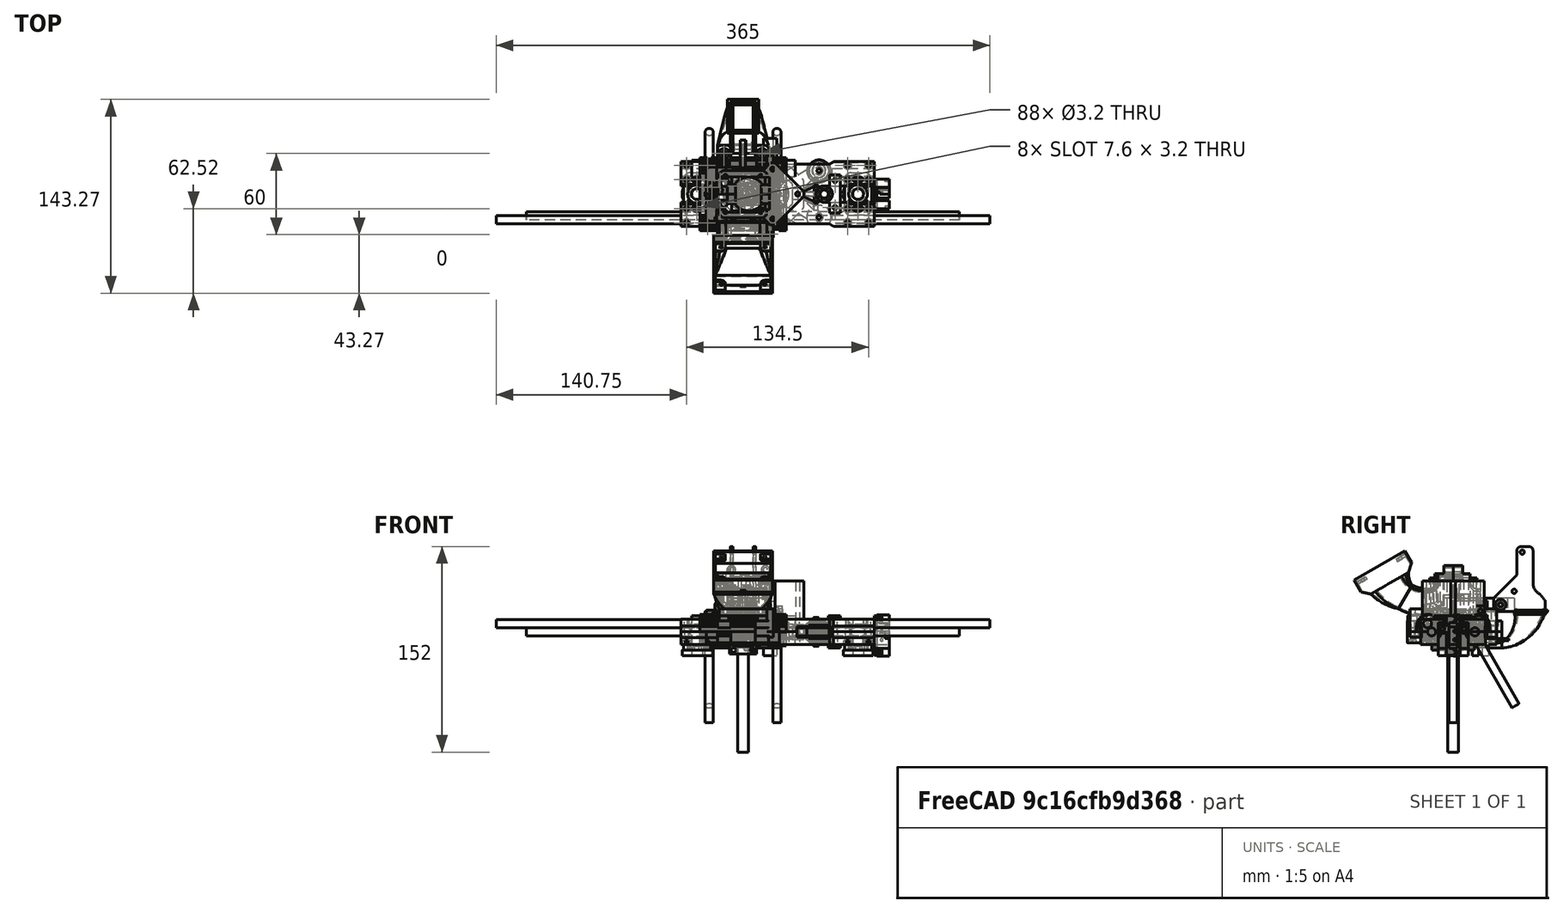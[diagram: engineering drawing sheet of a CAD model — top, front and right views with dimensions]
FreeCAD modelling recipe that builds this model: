
FCSTD DOCUMENT  (FreeCAD 0.18R15441 (Git))
Label: XZAxis_Assembly_A2PlusAddon
License: All rights reserved
LicenseURL: http://en.wikipedia.org/wiki/All_rights_reserved
objects: Part::FeaturePython×55, Part::Mirroring×15, App::Part×10, Part::Cylinder×5
note: 75 computed .brp shape members not serialized (recipe doc carries the construction recipe); baked Part::Feature solids carry a one-line shape summary decoded from their .brp

FEATURE [Part::FeaturePython] RightXEndHalf_Bottom_001  label="RightXEndHalf_Bottom"  # a2plus imported part (geometry in sourceFile) (typed FeaturePython)
  Placement = pos=(0,0,0) rot=(0,0,1;3.14159rad)
  a2p_Version = V0.1
  fixedPosition = true
  sourceFile = ./XAxis_Right/RightXEndHalf_Bottom.FCStd
  subassemblyImport = false
  timeLastImport = 1.54791e+09
  updateColors = true
FEATURE [Part::FeaturePython] RightXEndHalf_001  label="RightXEndHalf_Top"  # a2plus imported part (geometry in sourceFile) (typed FeaturePython)
  Placement = pos=(0,0,0) rot=(0,1,0;3.14159rad)
  a2p_Version = V0.1
  fixedPosition = true
  sourceFile = ./XAxis_Right/RightXEndHalf_Top.FCStd
  subassemblyImport = false
  timeLastImport = 1.54791e+09
  updateColors = true
FEATURE [Part::FeaturePython] RightXEnd_TensionerIdler_001  label="RightXEnd_TensionerIdler"  # a2plus imported part (geometry in sourceFile) (typed FeaturePython)
  a2p_Version = V0.1
  fixedPosition = true
  sourceFile = ./XAxis_Right/RightXEnd_TensionerIdler.FCStd
  subassemblyImport = false
  timeLastImport = 1.54602e+09
  updateColors = true
FEATURE [Part::FeaturePython] RightXEnd_TensionerKnob_001  label="RightXEnd_TensionerKnob"  # a2plus imported part (geometry in sourceFile) (typed FeaturePython)
  Placement = pos=(45.5,0,3.1e-15) rot=(0,1,0;1.5708rad)
  a2p_Version = V0.1
  fixedPosition = true
  sourceFile = ./XAxis_Right/RightXEnd_TensionerKnob.FCStd
  subassemblyImport = false
  timeLastImport = 1.54006e+09
  updateColors = true
FEATURE [Part::FeaturePython] RightXEnd_TensionerStand_001  label="RightXEnd_TensionerStand"  # a2plus imported part (geometry in sourceFile) (typed FeaturePython)
  Placement = pos=(36.825,-5e-15,0) rot=(0,0,1;3.14159rad)
  a2p_Version = V0.1
  fixedPosition = true
  sourceFile = ./XAxis_Right/RightXEnd_TensionerStand.FCStd
  subassemblyImport = false
  timeLastImport = 1.54596e+09
  updateColors = true
FEATURE [Part::FeaturePython] BeltPulley_2x685zz_FCGearAddon_001  label="BeltPulley_2x685zz_FCGearAddon"  # a2plus imported part (geometry in sourceFile) (typed FeaturePython)
  Placement = pos=(4,0,-3.5) rot=(0,0,1;0rad)
  a2p_Version = V0.1
  fixedPosition = true
  sourceFile = ./XAxis_Right/BeltPulley_2x685zz_FCGearAddon.FCStd
  subassemblyImport = false
  timeLastImport = 1.54006e+09
  updateColors = true
FEATURE [App::Part] Part001  label="RightIdlerPart"
  Group = -> [RightXEnd_TensionerIdler_001,BeltPulley_2x685zz_FCGearAddon_001]
  Origin = -> Origin001
  Placement = pos=(15,0,0) rot=(0,0,1;0rad)
FEATURE [Part::FeaturePython] BeltPulley_2x623zz_FCGearAddon_001  label="Right_BeltPulley_2x623zz_FCGearAddon"  # a2plus imported part (geometry in sourceFile) (typed FeaturePython)
  Placement = pos=(-5,-17.25,-3.25) rot=(0,0,1;0rad)
  a2p_Version = V0.1
  fixedPosition = true
  sourceFile = ./XAxis_Right/BeltPulley_2x623zz_FCGearAddon.FCStd
  subassemblyImport = false
  timeLastImport = 1.54602e+09
  updateColors = true
FEATURE [Part::Mirroring] Part__Mirroring  label="Right_BeltPulley_2x623zz_FCGearAddon_Mirror"
  Base = (0,0,0)
  Normal = (0,1,0)
  Source = -> BeltPulley_2x623zz_FCGearAddon_001
FEATURE [Part::FeaturePython] Rod_M6x320mm_001  label="XRod_M6x320mm"  # a2plus imported part (geometry in sourceFile) (typed FeaturePython)
  Placement = pos=(0,16,0) rot=(-1,0,0;1.5708rad)
  a2p_Version = V0.1
  fixedPosition = false
  sourceFile = ./Helpers/Rod_M6x320mm.FCStd
  subassemblyImport = false
  timeLastImport = 1.54611e+09
  updateColors = true
FEATURE [Part::Mirroring] Part__Mirroring001  label="XRod_M6x320mm_Mirror"
  Base = (0,0,0)
  Normal = (0,1,0)
  Source = -> Rod_M6x320mm_001
FEATURE [App::Part] Part003  label="XRods"
  Group = -> [Rod_M6x320mm_001,Part__Mirroring001]
  Origin = -> Origin003
FEATURE [Part::FeaturePython] LeftXEndHalf_Bottom_001  label="LeftXEndHalf_Bottom"  # a2plus imported part (geometry in sourceFile) (typed FeaturePython)
  a2p_Version = V0.1
  fixedPosition = false
  sourceFile = ./XAxis_Left/LeftXEndHalf_Bottom.FCStd
  subassemblyImport = false
  timeLastImport = 1.54791e+09
  updateColors = true
FEATURE [Part::FeaturePython] LeftXEndHalf_001  label="LeftXEndHalf_Top"  # a2plus imported part (geometry in sourceFile) (typed FeaturePython)
  Placement = pos=(0,0,0) rot=(1,0,0;3.14159rad)
  a2p_Version = V0.1
  fixedPosition = false
  sourceFile = ./XAxis_Left/LeftXEndHalf_Top.FCStd
  subassemblyImport = false
  timeLastImport = 1.54791e+09
  updateColors = true
FEATURE [Part::FeaturePython] BeltPulley_2x623zz_FCGearAddon_002  label="Left_BeltPulley_2x623zz_FCGearAddon"  # a2plus imported part (geometry in sourceFile) (typed FeaturePython)
  Placement = pos=(56.125,-17.25,-3.25) rot=(0,0,1;0rad)
  a2p_Version = V0.1
  fixedPosition = false
  sourceFile = ./XAxis_Right/BeltPulley_2x623zz_FCGearAddon.FCStd
  subassemblyImport = false
  timeLastImport = 1.54602e+09
  updateColors = true
FEATURE [Part::Mirroring] Part__Mirroring002  label="Left_BeltPulley_2x623zz_FCGearAddon (Mirror #3)"
  Base = (0,0,0)
  Normal = (0,1,0)
  Source = -> BeltPulley_2x623zz_FCGearAddon_002
FEATURE [Part::FeaturePython] CarriageHalf_Bottom_001  label="XCarriageHalf_Bottom"  # a2plus imported part (geometry in sourceFile) (typed FeaturePython)
  Placement = pos=(0,-1e-15,-8) rot=(1,0,0;3.14159rad)
  a2p_Version = V0.1
  fixedPosition = false
  sourceFile = ./XCarriage/CarriageHalf_Bottom.FCStd
  subassemblyImport = false
  timeLastImport = 1.54527e+09
  updateColors = true
FEATURE [Part::FeaturePython] CarriageHalf_001  label="XCarriageHalf_Top"  # a2plus imported part (geometry in sourceFile) (typed FeaturePython)
  Placement = pos=(0,0,8) rot=(0,0,1;3.14159rad)
  a2p_Version = V0.1
  fixedPosition = false
  sourceFile = ./XCarriage/CarriageHalf_Top.FCStd
  subassemblyImport = false
  timeLastImport = 1.54774e+09
  updateColors = true
FEATURE [Part::FeaturePython] LM6UU_IGUS_001  label="XBearing"  # a2plus imported part (geometry in sourceFile) (typed FeaturePython)
  Placement = pos=(-20.25,-16,-4e-15) rot=(0,1,0;1.5708rad)
  a2p_Version = V0.1
  fixedPosition = false
  sourceFile = ./Other/LM6UU_IGUS.fcstd
  subassemblyImport = false
  timeLastImport = 1.54524e+09
  updateColors = true
FEATURE [Part::Mirroring] Part__Mirroring003  label="XBearing_Mirror1_YZ"
  Base = (0,0,0)
  Normal = (1,0,0)
  Source = -> LM6UU_IGUS_001
FEATURE [Part::Mirroring] Part__Mirroring004  label="XBearing_Mirror1_XZ"
  Base = (0,0,0)
  Normal = (0,1,0)
  Source = -> LM6UU_IGUS_001
FEATURE [Part::Mirroring] Part__Mirroring005  label="XBearing_Mirror2_XZ"
  Base = (0,0,0)
  Normal = (0,1,0)
  Source = -> Part__Mirroring003
FEATURE [Part::FeaturePython] CarriageBeltClamp_001  label="XCarriageBeltClamp"  # a2plus imported part (geometry in sourceFile) (typed FeaturePython)
  Placement = pos=(-19,-34,-3) rot=(0,0,1;0rad)
  a2p_Version = V0.1
  fixedPosition = false
  sourceFile = ./XCarriage/CarriageBeltClamp.FCStd
  subassemblyImport = false
  timeLastImport = 1.54006e+09
  updateColors = true
FEATURE [Part::Mirroring] Part__Mirroring006  label="XCarriageBeltClamp_Mirror"
  Base = (0,0,0)
  Normal = (1,0,0)
  Source = -> CarriageBeltClamp_001
FEATURE [Part::FeaturePython] BearingClamp_001  label="LeftBearingClamp"  # a2plus imported part (geometry in sourceFile) (typed FeaturePython)
  Placement = pos=(66.1,0,0) rot=(0,0,1;0rad)
  a2p_Version = V0.1
  fixedPosition = false
  sourceFile = ./XAxis_Left/BearingClamp.FCStd
  subassemblyImport = false
  timeLastImport = 1.54786e+09
  updateColors = true
FEATURE [Part::FeaturePython] LeftBearingClamp_001  label="RightBearingClamp"  # a2plus imported part (geometry in sourceFile) (typed FeaturePython)
  Placement = pos=(-15.1,2e-15,0) rot=(0,0,1;3.14159rad)
  a2p_Version = V0.1
  fixedPosition = false
  sourceFile = ./XAxis_Left/BearingClamp.FCStd
  subassemblyImport = false
  timeLastImport = 1.54786e+09
  updateColors = true
FEATURE [Part::FeaturePython] HotendClippingLeftHalf_E3DV6_Bowden_001  label="HotendClippingLeftHalf_E3DV6_Bowden"  # a2plus imported part (geometry in sourceFile) (typed FeaturePython)
  Placement = pos=(0,0,8) rot=(0,0,1;0rad)
  a2p_Version = V0.1
  fixedPosition = false
  sourceFile = ./XCarriage/HotendClippingLeftHalf_E3DV6_Bowden.FCStd
  subassemblyImport = false
  timeLastImport = 1.54672e+09
  updateColors = true
FEATURE [Part::FeaturePython] HotendClippingRightHalf_E3DV6_Bowden_001  label="HotendClippingRightHalf_E3DV6_Bowden"  # a2plus imported part (geometry in sourceFile) (typed FeaturePython)
  Placement = pos=(0,0,8) rot=(0,0,1;0rad)
  a2p_Version = V0.1
  fixedPosition = false
  sourceFile = ./XCarriage/HotendClippingRightHalf_E3DV6_Bowden.FCStd
  subassemblyImport = false
  timeLastImport = 1.54679e+09
  updateColors = true
FEATURE [Part::FeaturePython] Hotend_E3D_Dummy_001  label="Hotend_E3D_Dummy"  # a2plus imported part (geometry in sourceFile) (typed FeaturePython)
  Placement = pos=(4,0,11.3) rot=(0,0,1;0rad)
  a2p_Version = V0.1
  fixedPosition = false
  sourceFile = ./Helpers/Hotend_E3D_Dummy.FCStd
  subassemblyImport = false
  timeLastImport = 1.54646e+09
  updateColors = true
FEATURE [Part::FeaturePython] Hotend_E3D_Dummy_Outer_001  label="Hotend_E3D_Dummy_Outer"  # a2plus imported part (geometry in sourceFile) (typed FeaturePython)
  Placement = pos=(4,0,11.3) rot=(0,0,1;0rad)
  a2p_Version = V0.1
  fixedPosition = false
  sourceFile = ./Helpers/Hotend_E3D_Dummy_Outer.FCStd
  subassemblyImport = false
  timeLastImport = 1.54656e+09
  updateColors = true
FEATURE [Part::Cylinder] Cylinder  label="ScrewTopCilinder1"
  Angle = 360
  AttacherType = Attacher::AttachEngine3D
  Height = 4
  Placement = pos=(-14,-30,8) rot=(0,0,1;0rad)
  Radius = 3.5
FEATURE [Part::Cylinder] Cylinder001  label="ScrewTopCilinder2"
  Angle = 360
  AttacherType = Attacher::AttachEngine3D
  Height = 4
  Placement = pos=(14,-30,8) rot=(0,0,1;0rad)
  Radius = 3.5
FEATURE [Part::FeaturePython] HotendFrontFanCase_40x40_001  label="HotendFrontFanCase_40x40"  # a2plus imported part (geometry in sourceFile) (typed FeaturePython)
  Placement = pos=(0,-21,21) rot=(0,0,1;0rad)
  a2p_Version = V0.1
  fixedPosition = false
  sourceFile = ./XCarriage/HotendFrontFanCase_40x40.FCStd
  subassemblyImport = false
  timeLastImport = 1.54722e+09
  updateColors = true
FEATURE [Part::FeaturePython] FrontFanCaseClip_40x40_001  label="FrontFanCaseClip_40x40"  # a2plus imported part (geometry in sourceFile) (typed FeaturePython)
  Placement = pos=(0,-20,21) rot=(0,0,1;3.14159rad)
  a2p_Version = V0.1
  fixedPosition = false
  sourceFile = ./XCarriage/FrontFanCaseClip_40x40.FCStd
  subassemblyImport = false
  timeLastImport = 1.54722e+09
  updateColors = true
FEATURE [Part::FeaturePython] BackClip_001  label="BackClip"  # a2plus imported part (geometry in sourceFile) (typed FeaturePython)
  Placement = pos=(2e-15,20,15) rot=(0,0,1;3.14159rad)
  a2p_Version = V0.1
  fixedPosition = false
  sourceFile = ./XCarriage/BackClip.FCStd
  subassemblyImport = false
  timeLastImport = 1.54724e+09
  updateColors = true
FEATURE [Part::FeaturePython] BackTurbineClip_001  label="BackTurbineClip"  # a2plus imported part (geometry in sourceFile) (typed FeaturePython)
  Placement = pos=(4e-15,30,15) rot=(0,0,1;3.14159rad)
  a2p_Version = V0.1
  fixedPosition = false
  sourceFile = ./XCarriage/BackTurbineClip.FCStd
  subassemblyImport = false
  timeLastImport = 1.54726e+09
  updateColors = true
FEATURE [Part::FeaturePython] BackTurbinePipe_TwoSides_001  label="BackTurbinePipe_TwoSides"  # a2plus imported part (geometry in sourceFile) (typed FeaturePython)
  Placement = pos=(4e-15,30,15) rot=(0,0,1;3.14159rad)
  a2p_Version = V0.1
  fixedPosition = false
  sourceFile = ./XCarriage/BackTurbinePipe_TwoSides.FCStd
  subassemblyImport = false
  timeLastImport = 1.54847e+09
  updateColors = true
FEATURE [App::Part] Part005  label="XCarriage"
  Group = -> [CarriageHalf_Bottom_001,CarriageHalf_001,LM6UU_IGUS_001,Part__Mirroring003,Part__Mirroring005,Part__Mirroring004,CarriageBeltClamp_001,Part__Mirroring006,HotendClippingLeftHalf_E3DV6_Bowden_001,HotendClippingRightHalf_E3DV6_Bowden_001,Hotend_E3D_Dummy_001,Hotend_E3D_Dummy_Outer_001,Cylinder,Cylinder001,HotendFrontFanCase_40x40_001,FrontFanCaseClip_40x40_001,BackClip_001,BackTurbineClip_001,+1 more]
  Origin = -> Origin005
FEATURE [Part::FeaturePython] ZThreaderRodClip_THSL_200_8D_001  label="LeftZThreaderRodClip_THSL-200-8D"  # a2plus imported part (geometry in sourceFile) (typed FeaturePython)
  Placement = pos=(85,0,-13.5) rot=(0,0,1;0rad)
  a2p_Version = V0.1
  fixedPosition = false
  sourceFile = ./XAxis_Left/ZThreaderRodClip_THSL-200-8D.FCStd
  subassemblyImport = false
  timeLastImport = 1.54751e+09
  updateColors = true
FEATURE [Part::FeaturePython] ZThreaderRodClip_THSL_200_8D_001001  label="RightZThreaderRodClip_THSL-200-8D"  # a2plus imported part (geometry in sourceFile) (typed FeaturePython)
  Placement = pos=(-34,0,-13.5) rot=(0,0,1;0rad)
  a2p_Version = V0.1
  fixedPosition = false
  sourceFile = ./XAxis_Left/ZThreaderRodClip_THSL-200-8D.FCStd
  subassemblyImport = false
  timeLastImport = 1.54751e+09
  updateColors = true
FEATURE [Part::FeaturePython] THSL_200_8D_001  label="LeftNut_THSL-200-8D"  # a2plus imported part (geometry in sourceFile) (typed FeaturePython)
  Placement = pos=(85,0,-17.5) rot=(0,0,1;0rad)
  a2p_Version = V0.1
  fixedPosition = false
  sourceFile = ./Helpers/THSL-200-8D_Nut.FCStd
  subassemblyImport = false
  timeLastImport = 1.54757e+09
  updateColors = true
FEATURE [Part::FeaturePython] LeftNut_THSL_200_8D_001  label="RightNut_THSL-200-8D"  # a2plus imported part (geometry in sourceFile) (typed FeaturePython)
  Placement = pos=(-34,0,-17.5) rot=(0,0,1;0rad)
  a2p_Version = V0.1
  fixedPosition = false
  sourceFile = ./Helpers/THSL-200-8D_Nut.FCStd
  subassemblyImport = false
  timeLastImport = 1.54757e+09
  updateColors = true
FEATURE [Part::FeaturePython] XBearing_001  label="RightZBearing"  # a2plus imported part (geometry in sourceFile) (typed FeaturePython)
  Placement = pos=(-9,0,-5e-15) rot=(0,0,1;0rad)
  a2p_Version = V0.1
  fixedPosition = false
  sourceFile = ./Other/LM6UU_IGUS.fcstd
  subassemblyImport = false
  timeLastImport = 1.54524e+09
  updateColors = true
FEATURE [Part::FeaturePython] RightZBearing_001  label="LeftZBearing"  # a2plus imported part (geometry in sourceFile) (typed FeaturePython)
  Placement = pos=(60,0,0) rot=(0,0,1;0rad)
  a2p_Version = V0.1
  fixedPosition = false
  sourceFile = ./Other/LM6UU_IGUS.fcstd
  subassemblyImport = false
  timeLastImport = 1.54524e+09
  updateColors = true
FEATURE [Part::FeaturePython] Huxley_Z_Motor_Bracket_001  label="RightMotorBracket"  # a2plus imported part (geometry in sourceFile) (typed FeaturePython)
  Placement = pos=(-18,-27.05,0) rot=(0,0,1;0rad)
  a2p_Version = V0.1
  fixedPosition = false
  sourceFile = ./Helpers/Huxley_Z_Motor_Bracket.FCStd
  subassemblyImport = false
  timeLastImport = 1.54757e+09
  updateColors = true
FEATURE [Part::FeaturePython] Nema14_Motor_001  label="RightMotor"  # a2plus imported part (geometry in sourceFile) (typed FeaturePython)
  Placement = pos=(0,1e-15,12) rot=(1,0,0;3.14159rad)
  a2p_Version = V0.1
  fixedPosition = false
  sourceFile = ./Helpers/Nema14_Motor.FCStd
  subassemblyImport = false
  timeLastImport = 1.54757e+09
  updateColors = true
FEATURE [Part::FeaturePython] Right_Motor_001  label="XMotor"  # a2plus imported part (geometry in sourceFile) (typed FeaturePython)
  Placement = pos=(21.885,2e-15,9.5) rot=(0.382683,0.92388,0;3.14159rad)
  a2p_Version = V0.1
  fixedPosition = false
  sourceFile = ./Helpers/Nema14_Motor.FCStd
  subassemblyImport = false
  timeLastImport = 1.54757e+09
  updateColors = true
FEATURE [Part::FeaturePython] Huxley_TopFrameVertex_001  label="RightFrameVertex"  # a2plus imported part (geometry in sourceFile) (typed FeaturePython)
  Placement = pos=(-32,-19.0525,6.00011) rot=(-0.250563,0.935113,-0.250563;1.63783rad)
  a2p_Version = V0.1
  fixedPosition = false
  sourceFile = ./Helpers/Huxley_TopFrameVertex.FCStd
  subassemblyImport = false
  timeLastImport = 1.54758e+09
  updateColors = true
FEATURE [Part::FeaturePython] Rod_M6x365mm_001  label="Top_Rod_M6x365mm"  # a2plus imported part (geometry in sourceFile) (typed FeaturePython)
  Placement = pos=(0,19.05,6) rot=(-1,0,0;1.5708rad)
  a2p_Version = V0.1
  fixedPosition = false
  sourceFile = ./Helpers/Rod_M6x365mm.FCStd
  subassemblyImport = false
  timeLastImport = 1.54758e+09
  updateColors = true
FEATURE [Part::Mirroring] Part__Mirroring007  label="Top_Rod_M6x365mm_Mirror"
  Base = (0,0,0)
  Normal = (0,1,0)
  Source = -> Rod_M6x365mm_001
FEATURE [App::Part] Part008  label="TopRods"
  Group = -> [Rod_M6x365mm_001,Part__Mirroring007]
  Origin = -> Origin008
  Placement = pos=(0,0,30) rot=(0,0,1;0rad)
FEATURE [Part::FeaturePython] Huxley_Z_Motor_Bracket_002  label="LeftMotorBracket"  # a2plus imported part (geometry in sourceFile) (typed FeaturePython)
  Placement = pos=(18,27.05,0) rot=(0,0,1;3.14159rad)
  a2p_Version = V0.1
  fixedPosition = false
  sourceFile = ./Helpers/Huxley_Z_Motor_Bracket.FCStd
  subassemblyImport = false
  timeLastImport = 1.54757e+09
  updateColors = true
FEATURE [Part::FeaturePython] Huxley_TopFrameVertex_002  label="LeftFrameVertex"  # a2plus imported part (geometry in sourceFile) (typed FeaturePython)
  Placement = pos=(32,19.05,6) rot=(-0.694747,-0.186157,0.694747;2.7735rad)
  a2p_Version = V0.1
  fixedPosition = false
  sourceFile = ./Helpers/Huxley_TopFrameVertex.FCStd
  subassemblyImport = false
  timeLastImport = 1.54758e+09
  updateColors = true
FEATURE [Part::FeaturePython] Nema14_Motor_002  label="LeftMotor"  # a2plus imported part (geometry in sourceFile) (typed FeaturePython)
  Placement = pos=(0,1e-15,12) rot=(1,0,0;3.14159rad)
  a2p_Version = V0.1
  fixedPosition = false
  sourceFile = ./Helpers/Nema14_Motor.FCStd
  subassemblyImport = false
  timeLastImport = 1.54757e+09
  updateColors = true
FEATURE [Part::Cylinder] Cylinder002  label="LeftTopRodNut"
  Angle = 360
  AttacherType = Attacher::AttachEngine3D
  Height = 6.5
  Placement = pos=(32,-19.05,6) rot=(0,1,0;1.5708rad)
  Radius = 6
FEATURE [Part::Mirroring] Part__Mirroring008  label="LeftTopRodNut_Mirror"
  Base = (0,0,0)
  Normal = (0,1,0)
  Source = -> Cylinder002
FEATURE [Part::Cylinder] Cylinder003  label="RightTopRodNut"
  Angle = 360
  AttacherType = Attacher::AttachEngine3D
  Height = 6.5
  Placement = pos=(-38,-19.05,6) rot=(0,1,0;1.5708rad)
  Radius = 6
FEATURE [Part::Mirroring] Part__Mirroring009  label="RightTopRodNut_Mirror"
  Base = (0,0,0)
  Normal = (0,1,0)
  Source = -> Cylinder003
FEATURE [Part::FeaturePython] Rod_M6x80mm_001  label="RightRod_M6x80mm"  # a2plus imported part (geometry in sourceFile) (typed FeaturePython)
  Placement = pos=(25,0,-27) rot=(0,1,0;1.5708rad)
  a2p_Version = V0.1
  fixedPosition = false
  sourceFile = ./Helpers/Rod_M6x80mm.FCStd
  subassemblyImport = false
  timeLastImport = 1.54757e+09
  updateColors = true
FEATURE [Part::FeaturePython] Rod_M6x80mm_002  label="LeftRod_M6x80mm"  # a2plus imported part (geometry in sourceFile) (typed FeaturePython)
  Placement = pos=(-25,0,-27) rot=(0,1,0;1.5708rad)
  a2p_Version = V0.1
  fixedPosition = false
  sourceFile = ./Helpers/Rod_M6x80mm.FCStd
  subassemblyImport = false
  timeLastImport = 1.54757e+09
  updateColors = true
FEATURE [Part::FeaturePython] Rod_M6x80mm_003  label="RightSideRod_M6x80mm"  # a2plus imported part (geometry in sourceFile) (typed FeaturePython)
  Placement = pos=(-25,-26.0167,-20.0622) rot=(-0.250563,0.935113,-0.250563;1.63783rad)
  a2p_Version = V0.1
  fixedPosition = false
  sourceFile = ./Helpers/Rod_M6x80mm.FCStd
  subassemblyImport = false
  timeLastImport = 1.54757e+09
  updateColors = true
FEATURE [Part::Mirroring] Part__Mirroring010  label="RightSideRod_M6x80mm_Mirror"
  Base = (0,0,0)
  Normal = (0,1,0)
  Source = -> Rod_M6x80mm_003
FEATURE [Part::FeaturePython] Rod_M6x80mm_004  label="LeftSideRod_M6x80mm"  # a2plus imported part (geometry in sourceFile) (typed FeaturePython)
  Placement = pos=(25,-26.0167,-20.0622) rot=(-0.250563,0.935113,-0.250563;1.63783rad)
  a2p_Version = V0.1
  fixedPosition = false
  sourceFile = ./Helpers/Rod_M6x80mm.FCStd
  subassemblyImport = false
  timeLastImport = 1.54757e+09
  updateColors = true
FEATURE [Part::Mirroring] Part__Mirroring011  label="LeftSideRod_M6x80mm_Mirror"
  Base = (0,0,0)
  Normal = (0,1,0)
  Source = -> Rod_M6x80mm_004
FEATURE [Part::FeaturePython] ZThreadedRodCoupler_THSL_200_8D_D8mm_001  label="RightZThreadedRodCoupler_THSL-200-8D"  # a2plus imported part (geometry in sourceFile) (typed FeaturePython)
  Placement = pos=(0,0,-16.5) rot=(0,0,1;0rad)
  a2p_Version = V0.1
  fixedPosition = false
  sourceFile = ./ZAxis/ZThreadedRodCoupler_THSL-200-8D_D8mm.FCStd
  subassemblyImport = false
  timeLastImport = 1.54006e+09
  updateColors = true
FEATURE [Part::Mirroring] Part__Mirroring012  label="RightZThreadedRodCoupler_THSL-200-8D_Mirror"
  Base = (0,0,0)
  Normal = (0,1,0)
  Source = -> ZThreadedRodCoupler_THSL_200_8D_D8mm_001
FEATURE [Part::FeaturePython] ZThreadedRodCoupler_THSL_200_8D_D8mm_002  label="LeftZThreadedRodCoupler_THSL-200-8D"  # a2plus imported part (geometry in sourceFile) (typed FeaturePython)
  Placement = pos=(0,0,-16.5) rot=(0,0,1;0rad)
  a2p_Version = V0.1
  fixedPosition = false
  sourceFile = ./ZAxis/ZThreadedRodCoupler_THSL-200-8D_D8mm.FCStd
  subassemblyImport = false
  timeLastImport = 1.54006e+09
  updateColors = true
FEATURE [Part::Mirroring] Part__Mirroring013  label="LeftZThreadedRodCoupler_THSL-200-8D_Mirror"
  Base = (0,0,0)
  Normal = (0,1,0)
  Source = -> ZThreadedRodCoupler_THSL_200_8D_D8mm_002
FEATURE [Part::FeaturePython] Rod_M8x80mm_001  label="LeftRod_M8x80mm"  # a2plus imported part (geometry in sourceFile) (typed FeaturePython)
  Placement = pos=(1.09e-14,0,-49) rot=(0,1,0;1.5708rad)
  a2p_Version = V0.1
  fixedPosition = false
  sourceFile = ./Helpers/Rod_M8x80mm.FCStd
  subassemblyImport = false
  timeLastImport = 1.54757e+09
  updateColors = true
FEATURE [App::Part] Part009  label="LeftMotorMount"
  Group = -> [Huxley_Z_Motor_Bracket_002,Nema14_Motor_002,Huxley_TopFrameVertex_002,Cylinder002,Part__Mirroring008,Rod_M6x80mm_002,Rod_M6x80mm_004,Part__Mirroring011,ZThreadedRodCoupler_THSL_200_8D_D8mm_002,Part__Mirroring013,Rod_M8x80mm_001]
  Origin = -> Origin009
  Placement = pos=(-141,0,30) rot=(0,0,1;0rad)
FEATURE [Part::FeaturePython] LeftRod_M8x80mm_001  label="RightRod_M8x80mm"  # a2plus imported part (geometry in sourceFile) (typed FeaturePython)
  Placement = pos=(1.09e-14,0,-49) rot=(0,1,0;1.5708rad)
  a2p_Version = V0.1
  fixedPosition = false
  sourceFile = ./Helpers/Rod_M8x80mm.FCStd
  subassemblyImport = false
  timeLastImport = 1.54757e+09
  updateColors = true
FEATURE [Part::FeaturePython] ZEndStopClip_001  label="RightZEndStopClip"  # a2plus imported part (geometry in sourceFile) (typed FeaturePython)
  Placement = pos=(20,8e-15,-4) rot=(0.707107,0.707107,0;3.14159rad)
  a2p_Version = V0.1
  fixedPosition = false
  sourceFile = ./ZAxis/ZEndStopClip.FCStd
  subassemblyImport = false
  timeLastImport = 1.54006e+09
  updateColors = true
FEATURE [Part::FeaturePython] ZEndStopClip2_001  label="RightZEndStopClip2"  # a2plus imported part (geometry in sourceFile) (typed FeaturePython)
  Placement = pos=(20,-4e-15,0) rot=(0,0,1;1.5708rad)
  a2p_Version = V0.1
  fixedPosition = false
  sourceFile = ./ZAxis/ZEndStopClip2.FCStd
  subassemblyImport = false
  timeLastImport = 1.54006e+09
  updateColors = true
FEATURE [Part::FeaturePython] OpticalEndstop_001  label="ZOpticalEndstop"  # a2plus imported part (geometry in sourceFile) (typed FeaturePython)
  Placement = pos=(20,20.15,-5) rot=(0.707107,0.707107,0;3.14159rad)
  a2p_Version = V0.1
  fixedPosition = false
  sourceFile = ./Helpers/OpticalEndstop.FCStd
  subassemblyImport = false
  timeLastImport = 1.5476e+09
  updateColors = true
FEATURE [App::Part] Part007  label="RightMotorMount"
  Group = -> [Huxley_Z_Motor_Bracket_001,Nema14_Motor_001,Huxley_TopFrameVertex_001,Cylinder003,Part__Mirroring009,Rod_M6x80mm_001,Rod_M6x80mm_003,Part__Mirroring010,ZThreadedRodCoupler_THSL_200_8D_D8mm_001,Part__Mirroring012,LeftRod_M8x80mm_001,ZEndStopClip_001,ZEndStopClip2_001,OpticalEndstop_001]
  Origin = -> Origin007
  Placement = pos=(141,0,30) rot=(0,0,1;0rad)
FEATURE [App::Part] Part006  label="ZAxis_Assembly"
  Group = -> [Part007,Part008,Part009]
  Origin = -> Origin006
FEATURE [Part::Cylinder] Cylinder004  label="BearingScrewTop"
  Angle = 360
  AttacherType = Attacher::AttachEngine3D
  Height = 4
  Placement = pos=(-5,17.25,9.5) rot=(0,0,1;0rad)
  Radius = 3
FEATURE [Part::FeaturePython] ZEndstopClip1_001  label="ZEndstopClip1"  # a2plus imported part (geometry in sourceFile) (typed FeaturePython)
  Placement = pos=(24,20.15,12.5) rot=(0,0,1;3.14159rad)
  a2p_Version = V0.1
  fixedPosition = false
  sourceFile = ./XAxis_Right/ZEndstopClip1.FCStd
  subassemblyImport = false
  timeLastImport = 1.54765e+09
  updateColors = true
FEATURE [Part::FeaturePython] ZEndstopClip2_001  label="ZEndstopClip2"  # a2plus imported part (geometry in sourceFile) (typed FeaturePython)
  Placement = pos=(11,20.15,12.5) rot=(0,0,1;1.5708rad)
  a2p_Version = V0.1
  fixedPosition = false
  sourceFile = ./XAxis_Right/ZEndstopClip2.FCStd
  subassemblyImport = false
  timeLastImport = 1.54765e+09
  updateColors = true
FEATURE [App::Part] Part  label="RightEndPart"
  Group = -> [RightXEndHalf_Bottom_001,RightXEndHalf_001,RightXEnd_TensionerStand_001,RightXEnd_TensionerKnob_001,Part001,BeltPulley_2x623zz_FCGearAddon_001,Part__Mirroring,LeftBearingClamp_001,ZThreaderRodClip_THSL_200_8D_001001,LeftNut_THSL_200_8D_001,XBearing_001,Cylinder004,ZEndstopClip1_001,ZEndstopClip2_001]
  Origin = -> Origin
  Placement = pos=(175,0,0) rot=(0,0,1;0rad)
FEATURE [Part::FeaturePython] XEndstopClip1_001  label="XEndstopClip1"  # a2plus imported part (geometry in sourceFile) (typed FeaturePython)
  Placement = pos=(99,-4e-15,-2.75) rot=(0.57735,0.57735,0.57735;2.0944rad)
  a2p_Version = V0.1
  fixedPosition = false
  sourceFile = ./XAxis_Left/XEndstopClip1.FCStd
  subassemblyImport = false
  timeLastImport = 1.54774e+09
  updateColors = true
FEATURE [Part::FeaturePython] XEndstopClip2_001  label="XEndstopClip2"  # a2plus imported part (geometry in sourceFile) (typed FeaturePython)
  Placement = pos=(99,-3,-2.75) rot=(0.57735,-0.57735,0.57735;4.18879rad)
  a2p_Version = V0.1
  fixedPosition = false
  sourceFile = ./XAxis_Left/XEndstopClip2.FCStd
  subassemblyImport = false
  timeLastImport = 1.54773e+09
  updateColors = true
FEATURE [Part::Mirroring] Part__Mirroring014  label="XEndstopClip2_Mirror"
  Base = (102.5,-2.38419e-07,-2.75)
  Normal = (0,1,-1.19209e-07)
  Source = -> XEndstopClip2_001
FEATURE [App::Part] Part004  label="LeftEndPart"
  Group = -> [LeftXEndHalf_Bottom_001,LeftXEndHalf_001,BeltPulley_2x623zz_FCGearAddon_002,Part__Mirroring002,BearingClamp_001,ZThreaderRodClip_THSL_200_8D_001,THSL_200_8D_001,RightZBearing_001,Right_Motor_001,XEndstopClip1_001,XEndstopClip2_001,Part__Mirroring014]
  Origin = -> Origin004
  Placement = pos=(-226,0,0) rot=(0,0,1;0rad)
FEATURE [App::Part] Part002  label="XAxis_Assembly"
  Group = -> [Part,Part003,Part004,Part005]
  Origin = -> Origin002
